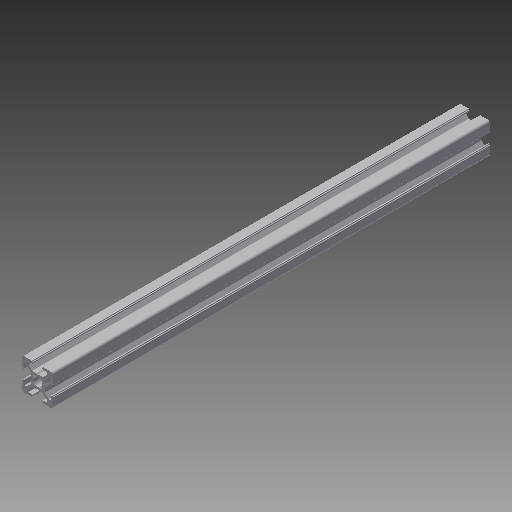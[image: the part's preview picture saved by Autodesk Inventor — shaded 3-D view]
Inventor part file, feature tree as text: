
AUTODESK INVENTOR PART (.ipt)
format: ipt  version: 2019 (Build 230136000, 136)  size: 308,224 bytes
history: native  units: in
note: dims shown in document units (in); Inventor stores cm internally (conversion verified against a paired STEP export)
features: other x3, extrude x1, sketch x1
ambient origin geometry x8: Origin, YZ Plane, XZ Plane, XY Plane, X Axis, Y Axis, Z Axis, Center Point
bodies: Solid1 (feature_tree)
feature tree (5):
  other  "Blocks"
  extrude  "Extrusion1"  Depth=1.0in
  sketch  "Sketch1"  dims[d1=0.0in d13=1.0in d14=1.0in]
  other  "20x20"
  other  "20x20:1"
